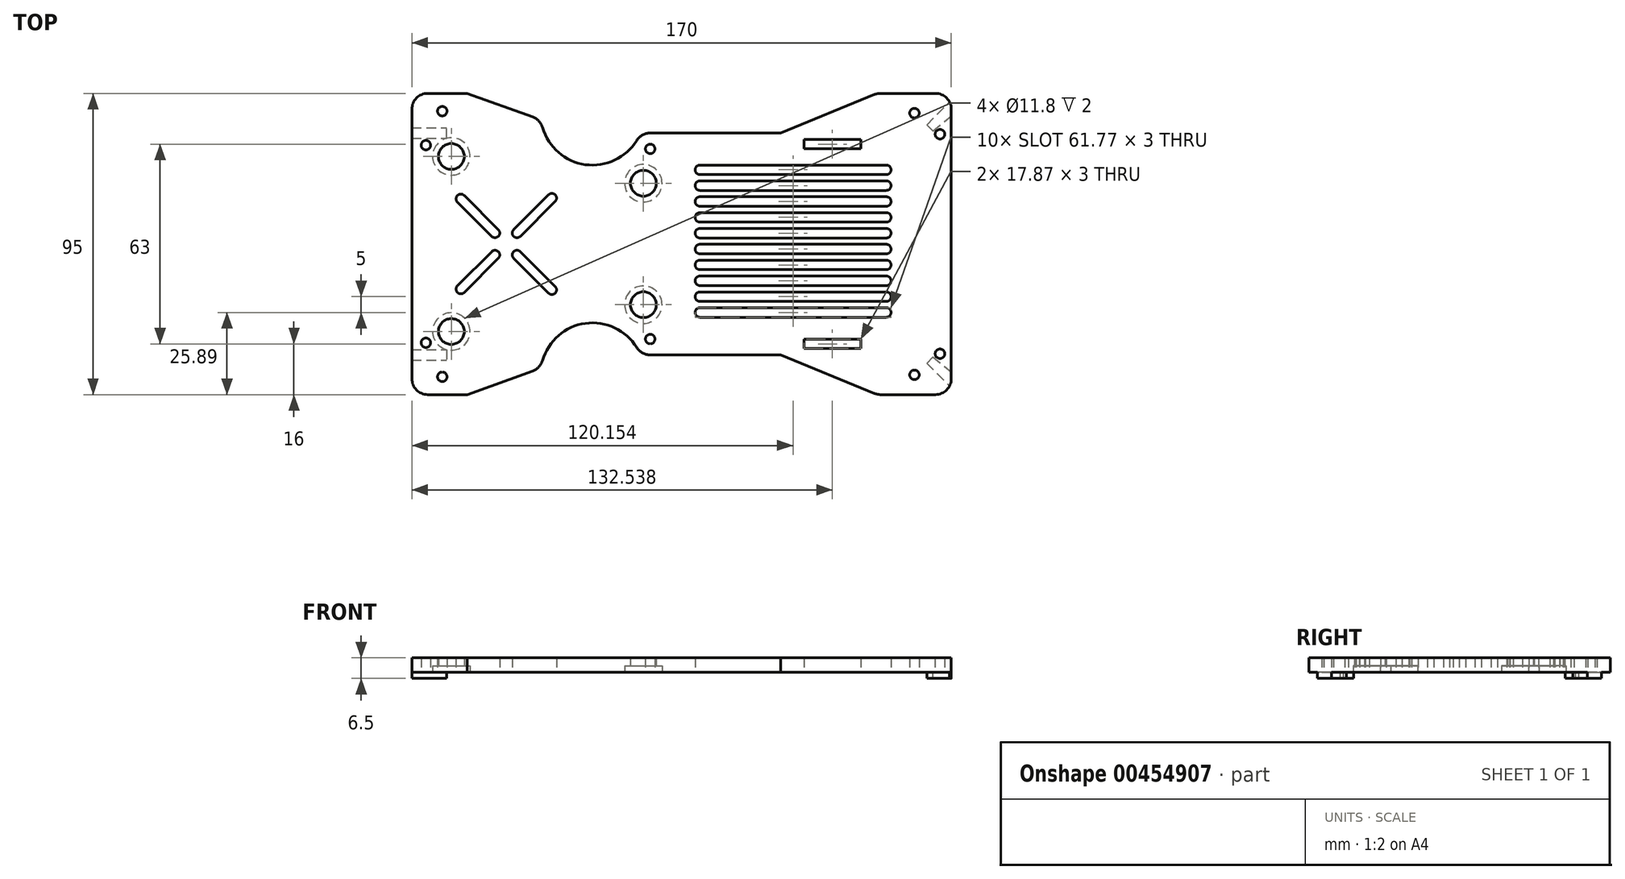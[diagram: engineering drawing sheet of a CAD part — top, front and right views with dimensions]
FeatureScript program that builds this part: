
annotation { "Feature Type Name" : "Feature", "Feature Type Description" : "" }
export const myFeature = defineFeature(function(context is Context, id is Id, definition is map)
    precondition{}
    {
        {
            var Q0;
            Q0=qCreatedBy(makeId("Top.planeOp"),FACE);
            var sketch = newSketch(context, id + "F0", { "sketchPlane" : qUnion([Q0])});
            skLineSegment(sketch, "E0.top", {"start": v(-158.33, 18) * mm, "end": v(-122.33, 18) * mm, "construction": true});
            skLineSegment(sketch, "E1.top", {"start": v(-2.46, 31.5) * mm, "end": v(-72.46, 31.5) * mm, "construction": true});
            skLineSegment(sketch, "E1.left", {"start": v(-2.46, 0) * mm, "end": v(-2.46, 31.5) * mm, "construction": true});
            skLineSegment(sketch, "E1.right", {"start": v(-72.46, 0) * mm, "end": v(-72.46, 31.5) * mm, "construction": true});
            skLineSegment(sketch, "E2.top", {"start": v(-5, 47.5) * mm, "end": v(-22.22, 47.5) * mm});
            skLineSegment(sketch, "E2.left", {"start": v(0, 35) * mm, "end": v(0, 42.5) * mm});
            skPoint(sketch, "E3.startSnap0", {"position": v(-23.2, 41.25) * mm});
            skPoint(sketch, "E3.startSnap1", {"position": v(-11.6, 47.5) * mm});
            skArc(sketch, "E4", {"start": v(-128.81, 36.72) * mm, "mid": v(-115.3, 25.02) * mm, "end": v(-99.14, 32.63) * mm});
            skLineSegment(sketch, "E5.trimOffspring", {"start": v(-94.88, 35) * mm, "end": v(-53.78, 35) * mm});
            skPoint(sketch, "E3.start.orphan", {"position": v(-11.6, 41.25) * mm});
            skCircle(sketch, "E6", {"center": v(-113.07, 41.25) * mm, "radius": 12.55 * mm, "construction": true});
            skLineSegment(sketch, "E7.top", {"start": v(-165, 47.5) * mm, "end": v(-149.65, 47.5) * mm});
            skLineSegment(sketch, "E7.left", {"start": v(-170, 35) * mm, "end": v(-170, 42.5) * mm});
            skLineSegment(sketch, "E8", {"start": v(-160.43, 41.87) * mm, "end": v(-136.46, 59) * mm, "construction": true});
            skPoint(sketch, "E8.startSnap0", {"position": v(-149.65, 47.5) * mm});
            skPoint(sketch, "E8.startSnap1", {"position": v(-170, 41.25) * mm});
            skLineSegment(sketch, "E9", {"start": v(-136.46, 59) * mm, "end": v(-62.44, 61.85) * mm, "construction": true});
            skLineSegment(sketch, "E10", {"start": v(-160.43, 41.87) * mm, "end": v(-62.44, 61.85) * mm, "construction": true});
            skCircle(sketch, "E11", {"center": v(-62.44, 61.85) * mm, "radius": 12.62 * mm, "construction": true});
            skLineSegment(sketch, "E12", {"start": v(-140.33, 0) * mm, "end": v(-158.33, 18) * mm, "construction": true});
            skLineSegment(sketch, "E13", {"start": v(-140.33, 0) * mm, "end": v(-122.33, 18) * mm, "construction": true});
            skArc(sketch, "E14", {"start": v(-153.5, 15.3) * mm, "mid": v(-155.63, 15.3) * mm, "end": v(-155.63, 13.18) * mm});
            skArc(sketch, "E15", {"start": v(-144.87, 2.42) * mm, "mid": v(-142.75, 2.42) * mm, "end": v(-142.75, 4.54) * mm});
            skArc(sketch, "E16", {"start": v(-137.91, 4.54) * mm, "mid": v(-137.91, 2.42) * mm, "end": v(-135.8, 2.42) * mm});
            skArc(sketch, "E17", {"start": v(-124.83, 13.38) * mm, "mid": v(-124.83, 15.5) * mm, "end": v(-126.95, 15.5) * mm});
            skLineSegment(sketch, "E18", {"start": v(-142.75, 4.54) * mm, "end": v(-153.5, 15.3) * mm});
            skLineSegment(sketch, "E19", {"start": v(-144.87, 2.42) * mm, "end": v(-155.63, 13.18) * mm});
            skLineSegment(sketch, "E20", {"start": v(-137.91, 4.54) * mm, "end": v(-126.95, 15.5) * mm});
            skLineSegment(sketch, "E21", {"start": v(-135.8, 2.42) * mm, "end": v(-124.83, 13.38) * mm});
            skLineSegment(sketch, "E22", {"start": v(-24.11, 47.13) * mm, "end": v(-53.78, 35) * mm});
            skCircle(sketch, "E23", {"center": v(-157.56, 27.6) * mm, "radius": 4.06 * mm});
            skCircle(sketch, "E24", {"center": v(-97.04, 19.15) * mm, "radius": 4.06 * mm});
            skPoint(sketch, "E2.bottom.end.orphan", {"position": v(-23.2, 35) * mm});
            skLineSegment(sketch, "E25.bottom", {"start": v(-28.53, 30) * mm, "end": v(-46.4, 30) * mm});
            skLineSegment(sketch, "E25.top", {"start": v(-28.53, 33) * mm, "end": v(-46.4, 33) * mm});
            skLineSegment(sketch, "E25.left", {"start": v(-28.53, 30) * mm, "end": v(-28.53, 33) * mm});
            skLineSegment(sketch, "E25.right", {"start": v(-46.4, 30) * mm, "end": v(-46.4, 33) * mm});
            skPoint(sketch, "E25.middle", {"position": v(-37.46, 31.5) * mm});
            skLineSegment(sketch, "E26", {"start": v(-131.92, 40.04) * mm, "end": v(-152.56, 47.5) * mm});
            skPoint(sketch, "E7.right.end.orphan", {"position": v(-129.3, 47.5) * mm});
            skPoint(sketch, "E27.visualSharp", {"position": v(-170, 47.5) * mm});
            skArc(sketch, "E27.filletArc", {"start": v(-165, 47.5) * mm, "mid": v(-168.54, 46.04) * mm, "end": v(-170, 42.5) * mm});
            skLineSegment(sketch, "E28", {"start": v(-2.46, 0) * mm, "end": v(-170, 0) * mm, "construction": true});
            skLineSegment(sketch, "E29", {"start": v(0, 35) * mm, "end": v(0, 0) * mm});
            skLineSegment(sketch, "E30", {"start": v(-170, 35) * mm, "end": v(-170, 0) * mm});
            skPoint(sketch, "E31.visualSharp", {"position": v(-129.3, 39.1) * mm});
            skArc(sketch, "E31.filletArc", {"start": v(-128.81, 36.72) * mm, "mid": v(-129.96, 38.75) * mm, "end": v(-131.92, 40.04) * mm});
            skPoint(sketch, "E32.visualSharp", {"position": v(-23.2, 47.5) * mm});
            skArc(sketch, "E32.filletArc", {"start": v(-22.22, 47.5) * mm, "mid": v(-23.19, 47.4) * mm, "end": v(-24.11, 47.13) * mm});
            skPoint(sketch, "E33.visualSharp", {"position": v(0, 47.5) * mm});
            skArc(sketch, "E33.filletArc", {"start": v(0, 42.5) * mm, "mid": v(-1.46, 46.04) * mm, "end": v(-5, 47.5) * mm});
            skPoint(sketch, "E34.visualSharp", {"position": v(-97.92, 35) * mm});
            skArc(sketch, "E34.filletArc", {"start": v(-94.88, 35) * mm, "mid": v(-97.32, 34.37) * mm, "end": v(-99.14, 32.63) * mm});
            skCircle(sketch, "E35", {"center": v(-94.88, 30) * mm, "radius": 1.5 * mm});
            skCircle(sketch, "E36", {"center": v(-165.6, 31.16) * mm, "radius": 1.5 * mm});
            skCircle(sketch, "E37", {"center": v(-3.57, 34.62) * mm, "radius": 1.5 * mm});
            skArc(sketch, "E38.MirrorCS", {"start": v(-22.22, -47.5) * mm, "mid": v(-23.19, -47.4) * mm, "end": v(-24.11, -47.13) * mm});
            skCircle(sketch, "E39.MirrorC", {"center": v(-94.88, -30) * mm, "radius": 1.5 * mm});
            skArc(sketch, "E40.MirrorCS", {"start": v(-137.91, -4.54) * mm, "mid": v(-137.91, -2.42) * mm, "end": v(-135.8, -2.42) * mm});
            skArc(sketch, "E41.MirrorCS", {"start": v(-144.87, -2.42) * mm, "mid": v(-142.75, -2.42) * mm, "end": v(-142.75, -4.54) * mm});
            skLineSegment(sketch, "E42.MirrorCS", {"start": v(-28.53, -30) * mm, "end": v(-28.53, -33) * mm});
            skArc(sketch, "E43.MirrorCS", {"start": v(-153.5, -15.3) * mm, "mid": v(-155.63, -15.3) * mm, "end": v(-155.63, -13.18) * mm});
            skArc(sketch, "E44.MirrorCS", {"start": v(-94.88, -35) * mm, "mid": v(-97.32, -34.37) * mm, "end": v(-99.14, -32.63) * mm});
            skLineSegment(sketch, "E45.MirrorCS", {"start": v(-46.4, -30) * mm, "end": v(-46.4, -33) * mm});
            skArc(sketch, "E46.MirrorCS", {"start": v(-124.83, -13.38) * mm, "mid": v(-124.83, -15.5) * mm, "end": v(-126.95, -15.5) * mm});
            skArc(sketch, "E47.MirrorCS", {"start": v(-128.81, -36.72) * mm, "mid": v(-129.96, -38.75) * mm, "end": v(-131.92, -40.04) * mm});
            skArc(sketch, "E48.MirrorCS", {"start": v(-165, -47.5) * mm, "mid": v(-168.54, -46.04) * mm, "end": v(-170, -42.5) * mm});
            skCircle(sketch, "E49.MirrorC", {"center": v(-3.57, -34.62) * mm, "radius": 1.5 * mm});
            skArc(sketch, "E50.MirrorCS", {"start": v(0, -42.5) * mm, "mid": v(-1.46, -46.04) * mm, "end": v(-5, -47.5) * mm});
            skCircle(sketch, "E51.MirrorC", {"center": v(-165.6, -31.16) * mm, "radius": 1.5 * mm});
            skLineSegment(sketch, "E52.MirrorCS", {"start": v(-170, -35) * mm, "end": v(-170, -42.5) * mm});
            skLineSegment(sketch, "E53.MirrorCS", {"start": v(-2.46, -31.5) * mm, "end": v(-72.46, -31.5) * mm, "construction": true});
            skLineSegment(sketch, "E54.MirrorCS", {"start": v(-24.11, -47.13) * mm, "end": v(-53.78, -35) * mm});
            skLineSegment(sketch, "E55.MirrorCS", {"start": v(-165, -47.5) * mm, "end": v(-149.65, -47.5) * mm});
            skCircle(sketch, "E56.MirrorC", {"center": v(-157.56, -27.6) * mm, "radius": 4.06 * mm});
            skLineSegment(sketch, "E57.MirrorCS", {"start": v(-135.8, -2.42) * mm, "end": v(-124.83, -13.38) * mm});
            skPoint(sketch, "E58.MirrorP", {"position": v(-37.46, -31.5) * mm});
            skPoint(sketch, "E59.MirrorP", {"position": v(-23.2, -35) * mm});
            skPoint(sketch, "E60.MirrorP", {"position": v(-129.3, -39.1) * mm});
            skPoint(sketch, "E61.MirrorP", {"position": v(-11.6, -41.25) * mm});
            skLineSegment(sketch, "E62.MirrorCS", {"start": v(-72.46, 0) * mm, "end": v(-72.46, -31.5) * mm, "construction": true});
            skLineSegment(sketch, "E63.MirrorCS", {"start": v(-5, -47.5) * mm, "end": v(-22.22, -47.5) * mm});
            skLineSegment(sketch, "E64.MirrorCS", {"start": v(-94.88, -35) * mm, "end": v(-53.78, -35) * mm});
            skArc(sketch, "E65.MirrorCS", {"start": v(-128.81, -36.72) * mm, "mid": v(-115.3, -25.02) * mm, "end": v(-99.14, -32.63) * mm});
            skPoint(sketch, "E66.MirrorP", {"position": v(-149.65, -47.5) * mm});
            skPoint(sketch, "E67.MirrorP", {"position": v(-23.2, -47.5) * mm});
            skLineSegment(sketch, "E68.MirrorCS", {"start": v(-170, -35) * mm, "end": v(-170, 0) * mm});
            skLineSegment(sketch, "E69.MirrorCS", {"start": v(0, -35) * mm, "end": v(0, -42.5) * mm});
            skPoint(sketch, "E70.MirrorP", {"position": v(-129.3, -47.5) * mm});
            skCircle(sketch, "E71.MirrorC", {"center": v(-113.07, -41.25) * mm, "radius": 12.55 * mm, "construction": true});
            skLineSegment(sketch, "E72.MirrorCS", {"start": v(-160.43, -41.87) * mm, "end": v(-136.46, -59) * mm, "construction": true});
            skLineSegment(sketch, "E73.MirrorCS", {"start": v(-158.33, -18) * mm, "end": v(-122.33, -18) * mm, "construction": true});
            skPoint(sketch, "E74.MirrorP", {"position": v(0, -47.5) * mm});
            skLineSegment(sketch, "E75.MirrorCS", {"start": v(-131.92, -40.04) * mm, "end": v(-152.56, -47.5) * mm});
            skPoint(sketch, "E76.MirrorP", {"position": v(-11.6, -47.5) * mm});
            skLineSegment(sketch, "E77.MirrorCS", {"start": v(-140.33, 0) * mm, "end": v(-122.33, -18) * mm, "construction": true});
            skLineSegment(sketch, "E78.MirrorCS", {"start": v(-2.46, 0) * mm, "end": v(-2.46, -31.5) * mm, "construction": true});
            skLineSegment(sketch, "E79.MirrorCS", {"start": v(-28.53, -30) * mm, "end": v(-46.4, -30) * mm});
            skPoint(sketch, "E80.MirrorP", {"position": v(-170, -41.25) * mm});
            skLineSegment(sketch, "E81.MirrorCS", {"start": v(-140.33, 0) * mm, "end": v(-158.33, -18) * mm, "construction": true});
            skLineSegment(sketch, "E82.MirrorCS", {"start": v(-28.53, -33) * mm, "end": v(-46.4, -33) * mm});
            skPoint(sketch, "E83.MirrorP", {"position": v(-97.92, -35) * mm});
            skLineSegment(sketch, "E84.MirrorCS", {"start": v(-160.43, -41.87) * mm, "end": v(-62.44, -61.85) * mm, "construction": true});
            skLineSegment(sketch, "E85.MirrorCS", {"start": v(0, -35) * mm, "end": v(0, 0) * mm});
            skLineSegment(sketch, "E86.MirrorCS", {"start": v(-136.46, -59) * mm, "end": v(-62.44, -61.85) * mm, "construction": true});
            skPoint(sketch, "E87.MirrorP", {"position": v(-170, -47.5) * mm});
            skCircle(sketch, "E88.MirrorC", {"center": v(-97.04, -19.15) * mm, "radius": 4.06 * mm});
            skLineSegment(sketch, "E89.MirrorCS", {"start": v(-142.75, -4.54) * mm, "end": v(-153.5, -15.3) * mm});
            skLineSegment(sketch, "E90.MirrorCS", {"start": v(-137.91, -4.54) * mm, "end": v(-126.95, -15.5) * mm});
            skLineSegment(sketch, "E91.MirrorCS", {"start": v(-144.87, -2.42) * mm, "end": v(-155.63, -13.18) * mm});
            skCircle(sketch, "E92.MirrorC", {"center": v(-62.44, -61.85) * mm, "radius": 12.62 * mm, "construction": true});
            skCircle(sketch, "E93", {"center": v(-11.6, 41.25) * mm, "radius": 1.5 * mm});
            skCircle(sketch, "E94", {"center": v(-160.43, 41.87) * mm, "radius": 1.5 * mm});
            skCircle(sketch, "E95.MirrorC", {"center": v(-11.6, -41.25) * mm, "radius": 1.5 * mm});
            skCircle(sketch, "E96.MirrorC", {"center": v(-160.43, -41.87) * mm, "radius": 1.5 * mm});
            skSolve(sketch);
        }
        {
            var Q0;
            Q0 = qSketchRegion(id + "F0", true);
            extrude(context, id + "F1", {"entities" : qUnion([Q0]), "depth" : 4.5 * mm});
        }
        {
            var Q0;
            Q0=makeQuery(id+"F1.opExtrude","CAP_FACE",FACE,{"disambiguationData":[OSD([sQuery(id+"F0.wireOp",EDGE,"E2.top"),sQuery(id+"F0.wireOp",EDGE,"E2.left"),sQuery(id+"F0.wireOp",EDGE,"E4"),sQuery(id+"F0.wireOp",EDGE,"E5.trimOffspring"),sQuery(id+"F0.wireOp",EDGE,"E7.top"),sQuery(id+"F0.wireOp",EDGE,"E7.left"),sQuery(id+"F0.wireOp",EDGE,"E14"),sQuery(id+"F0.wireOp",EDGE,"E15"),sQuery(id+"F0.wireOp",EDGE,"E16"),sQuery(id+"F0.wireOp",EDGE,"E17"),sQuery(id+"F0.wireOp",EDGE,"E18"),sQuery(id+"F0.wireOp",EDGE,"E19"),sQuery(id+"F0.wireOp",EDGE,"E20"),sQuery(id+"F0.wireOp",EDGE,"E21"),sQuery(id+"F0.wireOp",EDGE,"E22"),sQuery(id+"F0.wireOp",EDGE,"E23"),sQuery(id+"F0.wireOp",EDGE,"E24"),sQuery(id+"F0.wireOp",EDGE,"E25.bottom"),sQuery(id+"F0.wireOp",EDGE,"E25.top"),sQuery(id+"F0.wireOp",EDGE,"E25.left"),sQuery(id+"F0.wireOp",EDGE,"E25.right"),sQuery(id+"F0.wireOp",EDGE,"E26"),sQuery(id+"F0.wireOp",EDGE,"E27.filletArc"),sQuery(id+"F0.wireOp",EDGE,"E29"),sQuery(id+"F0.wireOp",EDGE,"E30"),sQuery(id+"F0.wireOp",EDGE,"E31.filletArc"),sQuery(id+"F0.wireOp",EDGE,"E32.filletArc"),sQuery(id+"F0.wireOp",EDGE,"E33.filletArc"),sQuery(id+"F0.wireOp",EDGE,"E34.filletArc"),sQuery(id+"F0.wireOp",EDGE,"E35"),sQuery(id+"F0.wireOp",EDGE,"E36"),sQuery(id+"F0.wireOp",EDGE,"E37"),sQuery(id+"F0.wireOp",EDGE,"dc92d004-a6ad-41b4-b321-0510745f16cf0.MirrorC"),sQuery(id+"F0.wireOp",EDGE,"E38.MirrorCS"),sQuery(id+"F0.wireOp",EDGE,"E39.MirrorC"),sQuery(id+"F0.wireOp",EDGE,"E40.MirrorCS"),sQuery(id+"F0.wireOp",EDGE,"E41.MirrorCS"),sQuery(id+"F0.wireOp",EDGE,"E42.MirrorCS"),sQuery(id+"F0.wireOp",EDGE,"E43.MirrorCS"),sQuery(id+"F0.wireOp",EDGE,"E44.MirrorCS"),sQuery(id+"F0.wireOp",EDGE,"E45.MirrorCS"),sQuery(id+"F0.wireOp",EDGE,"E46.MirrorCS"),sQuery(id+"F0.wireOp",EDGE,"E47.MirrorCS"),sQuery(id+"F0.wireOp",EDGE,"E48.MirrorCS"),sQuery(id+"F0.wireOp",EDGE,"E49.MirrorC"),sQuery(id+"F0.wireOp",EDGE,"E50.MirrorCS"),sQuery(id+"F0.wireOp",EDGE,"E51.MirrorC"),sQuery(id+"F0.wireOp",EDGE,"E52.MirrorCS"),sQuery(id+"F0.wireOp",EDGE,"E54.MirrorCS"),sQuery(id+"F0.wireOp",EDGE,"E55.MirrorCS"),sQuery(id+"F0.wireOp",EDGE,"E56.MirrorC"),sQuery(id+"F0.wireOp",EDGE,"E57.MirrorCS"),sQuery(id+"F0.wireOp",EDGE,"E63.MirrorCS"),sQuery(id+"F0.wireOp",EDGE,"E64.MirrorCS"),sQuery(id+"F0.wireOp",EDGE,"E65.MirrorCS"),sQuery(id+"F0.wireOp",EDGE,"E68.MirrorCS"),sQuery(id+"F0.wireOp",EDGE,"E69.MirrorCS"),sQuery(id+"F0.wireOp",EDGE,"E75.MirrorCS"),sQuery(id+"F0.wireOp",EDGE,"E79.MirrorCS"),sQuery(id+"F0.wireOp",EDGE,"E82.MirrorCS"),sQuery(id+"F0.wireOp",EDGE,"E85.MirrorCS"),sQuery(id+"F0.wireOp",EDGE,"E88.MirrorC"),sQuery(id+"F0.wireOp",EDGE,"E89.MirrorCS"),sQuery(id+"F0.wireOp",EDGE,"E90.MirrorCS"),sQuery(id+"F0.wireOp",EDGE,"E91.MirrorCS"),sQuery(id+"F0.wireOp",EDGE,"E93"),sQuery(id+"F0.wireOp",EDGE,"E94"),sQuery(id+"F0.wireOp",EDGE,"E95.MirrorC"),sQuery(id+"F0.wireOp",EDGE,"E96.MirrorC")])],"isStart":true});
            var sketch = newSketch(context, id + "F2", { "sketchPlane" : qUnion([Q0])});
            skLineSegment(sketch, "E97.bottom", {"start": v(-170, 33.34) * mm, "end": v(-159, 33.34) * mm});
            skLineSegment(sketch, "E97.top", {"start": v(-170, 36.59) * mm, "end": v(-159, 36.59) * mm});
            skLineSegment(sketch, "E97.left", {"start": v(-170, 33.34) * mm, "end": v(-170, 36.59) * mm});
            skLineSegment(sketch, "E97.right", {"start": v(-159, 33.34) * mm, "end": v(-159, 36.59) * mm});
            skLineSegment(sketch, "E98", {"start": v(-160.43, 41.87) * mm, "end": v(-160.43, 36.87) * mm, "construction": true});
            skLineSegment(sketch, "E99", {"start": v(-11.6, 41.25) * mm, "end": v(-8.07, 37.71) * mm, "construction": true});
            skLineSegment(sketch, "E100", {"start": v(-11.6, 41.25) * mm, "end": v(0, 41.25) * mm, "construction": true});
            skLineSegment(sketch, "E101", {"start": v(-7.7, 37.6) * mm, "end": v(-0.54, 44.75) * mm});
            skLineSegment(sketch, "E102", {"start": v(-7.7, 37.6) * mm, "end": v(-5.77, 35.67) * mm});
            skLineSegment(sketch, "E103", {"start": v(-5.77, 35.67) * mm, "end": v(0, 40.31) * mm});
            skArc(sketch, "E104.0", {"start": v(0, 42.5) * mm, "mid": v(-0.14, 43.66) * mm, "end": v(-0.54, 44.75) * mm});
            skLineSegment(sketch, "E105.0", {"start": v(0, 40.31) * mm, "end": v(0, 42.5) * mm});
            skPoint(sketch, "E106.orphan", {"position": v(-5, 47.5) * mm});
            skPoint(sketch, "E107.orphan", {"position": v(0, -42.5) * mm});
            skLineSegment(sketch, "E108", {"start": v(-170, 0) * mm, "end": v(0, 0) * mm, "construction": true});
            skLineSegment(sketch, "E109.MirrorCS", {"start": v(0, -40.31) * mm, "end": v(0, -42.5) * mm});
            skArc(sketch, "E110.MirrorCS", {"start": v(0, -42.5) * mm, "mid": v(-0.14, -43.66) * mm, "end": v(-0.54, -44.75) * mm});
            skLineSegment(sketch, "E111.MirrorCS", {"start": v(-7.7, -37.6) * mm, "end": v(-5.77, -35.67) * mm});
            skLineSegment(sketch, "E112.MirrorCS", {"start": v(-170, -33.34) * mm, "end": v(-170, -36.59) * mm});
            skLineSegment(sketch, "E113.MirrorCS", {"start": v(-159, -33.34) * mm, "end": v(-159, -36.59) * mm});
            skLineSegment(sketch, "E114.MirrorCS", {"start": v(-11.6, -41.25) * mm, "end": v(-8.07, -37.71) * mm, "construction": true});
            skLineSegment(sketch, "E115.MirrorCS", {"start": v(-5.77, -35.67) * mm, "end": v(0, -40.31) * mm});
            skLineSegment(sketch, "E116.MirrorCS", {"start": v(-11.6, -41.25) * mm, "end": v(0, -41.25) * mm, "construction": true});
            skLineSegment(sketch, "E117.MirrorCS", {"start": v(-160.43, -41.87) * mm, "end": v(-160.43, -36.87) * mm, "construction": true});
            skLineSegment(sketch, "E118.MirrorCS", {"start": v(-7.7, -37.6) * mm, "end": v(-0.54, -44.75) * mm});
            skPoint(sketch, "E119.MirrorP", {"position": v(-5, -47.5) * mm});
            skLineSegment(sketch, "E120.MirrorCS", {"start": v(-170, -33.34) * mm, "end": v(-159, -33.34) * mm});
            skLineSegment(sketch, "E121.MirrorCS", {"start": v(-170, -36.59) * mm, "end": v(-159, -36.59) * mm});
            skSolve(sketch);
        }
        {
            var Q0;
            Q0 = qSketchRegion(id + "F2", true);
            extrude(context, id + "F3", {"entities" : qUnion([Q0]), "operationType" : NewBodyOperationType.ADD, "depth" : 2 * mm});
        }
        {
            var Q0;
            Q0=makeQuery(id+"F1.opExtrude","CAP_FACE",FACE,{"disambiguationData":[OSD([sQuery(id+"F0.wireOp",EDGE,"E2.top"),sQuery(id+"F0.wireOp",EDGE,"E2.left"),sQuery(id+"F0.wireOp",EDGE,"E4"),sQuery(id+"F0.wireOp",EDGE,"E5.trimOffspring"),sQuery(id+"F0.wireOp",EDGE,"E7.top"),sQuery(id+"F0.wireOp",EDGE,"E7.left"),sQuery(id+"F0.wireOp",EDGE,"E14"),sQuery(id+"F0.wireOp",EDGE,"E15"),sQuery(id+"F0.wireOp",EDGE,"E16"),sQuery(id+"F0.wireOp",EDGE,"E17"),sQuery(id+"F0.wireOp",EDGE,"E18"),sQuery(id+"F0.wireOp",EDGE,"E19"),sQuery(id+"F0.wireOp",EDGE,"E20"),sQuery(id+"F0.wireOp",EDGE,"E21"),sQuery(id+"F0.wireOp",EDGE,"E22"),sQuery(id+"F0.wireOp",EDGE,"E23"),sQuery(id+"F0.wireOp",EDGE,"E24"),sQuery(id+"F0.wireOp",EDGE,"E25.bottom"),sQuery(id+"F0.wireOp",EDGE,"E25.top"),sQuery(id+"F0.wireOp",EDGE,"E25.left"),sQuery(id+"F0.wireOp",EDGE,"E25.right"),sQuery(id+"F0.wireOp",EDGE,"E26"),sQuery(id+"F0.wireOp",EDGE,"E27.filletArc"),sQuery(id+"F0.wireOp",EDGE,"E29"),sQuery(id+"F0.wireOp",EDGE,"E30"),sQuery(id+"F0.wireOp",EDGE,"E31.filletArc"),sQuery(id+"F0.wireOp",EDGE,"E32.filletArc"),sQuery(id+"F0.wireOp",EDGE,"E33.filletArc"),sQuery(id+"F0.wireOp",EDGE,"E34.filletArc"),sQuery(id+"F0.wireOp",EDGE,"E35"),sQuery(id+"F0.wireOp",EDGE,"E36"),sQuery(id+"F0.wireOp",EDGE,"E37"),sQuery(id+"F0.wireOp",EDGE,"dc92d004-a6ad-41b4-b321-0510745f16cf0.MirrorC"),sQuery(id+"F0.wireOp",EDGE,"E38.MirrorCS"),sQuery(id+"F0.wireOp",EDGE,"E39.MirrorC"),sQuery(id+"F0.wireOp",EDGE,"E40.MirrorCS"),sQuery(id+"F0.wireOp",EDGE,"E41.MirrorCS"),sQuery(id+"F0.wireOp",EDGE,"E42.MirrorCS"),sQuery(id+"F0.wireOp",EDGE,"E43.MirrorCS"),sQuery(id+"F0.wireOp",EDGE,"E44.MirrorCS"),sQuery(id+"F0.wireOp",EDGE,"E45.MirrorCS"),sQuery(id+"F0.wireOp",EDGE,"E46.MirrorCS"),sQuery(id+"F0.wireOp",EDGE,"E47.MirrorCS"),sQuery(id+"F0.wireOp",EDGE,"E48.MirrorCS"),sQuery(id+"F0.wireOp",EDGE,"E49.MirrorC"),sQuery(id+"F0.wireOp",EDGE,"E50.MirrorCS"),sQuery(id+"F0.wireOp",EDGE,"E51.MirrorC"),sQuery(id+"F0.wireOp",EDGE,"E52.MirrorCS"),sQuery(id+"F0.wireOp",EDGE,"E54.MirrorCS"),sQuery(id+"F0.wireOp",EDGE,"E55.MirrorCS"),sQuery(id+"F0.wireOp",EDGE,"E56.MirrorC"),sQuery(id+"F0.wireOp",EDGE,"E57.MirrorCS"),sQuery(id+"F0.wireOp",EDGE,"E63.MirrorCS"),sQuery(id+"F0.wireOp",EDGE,"E64.MirrorCS"),sQuery(id+"F0.wireOp",EDGE,"E65.MirrorCS"),sQuery(id+"F0.wireOp",EDGE,"E68.MirrorCS"),sQuery(id+"F0.wireOp",EDGE,"E69.MirrorCS"),sQuery(id+"F0.wireOp",EDGE,"E75.MirrorCS"),sQuery(id+"F0.wireOp",EDGE,"E79.MirrorCS"),sQuery(id+"F0.wireOp",EDGE,"E82.MirrorCS"),sQuery(id+"F0.wireOp",EDGE,"E85.MirrorCS"),sQuery(id+"F0.wireOp",EDGE,"E88.MirrorC"),sQuery(id+"F0.wireOp",EDGE,"E89.MirrorCS"),sQuery(id+"F0.wireOp",EDGE,"E90.MirrorCS"),sQuery(id+"F0.wireOp",EDGE,"E91.MirrorCS"),sQuery(id+"F0.wireOp",EDGE,"E93"),sQuery(id+"F0.wireOp",EDGE,"E94"),sQuery(id+"F0.wireOp",EDGE,"E95.MirrorC"),sQuery(id+"F0.wireOp",EDGE,"E96.MirrorC")])],"isStart":true});
            var sketch = newSketch(context, id + "F4", { "sketchPlane" : qUnion([Q0])});
            skCircle(sketch, "E122", {"center": v(-97.04, 19.15) * mm, "radius": 5.9 * mm});
            skCircle(sketch, "E123", {"center": v(-157.56, 27.6) * mm, "radius": 5.9 * mm});
            skCircle(sketch, "E124", {"center": v(-97.04, -19.15) * mm, "radius": 5.9 * mm});
            skCircle(sketch, "E125", {"center": v(-157.56, -27.6) * mm, "radius": 5.9 * mm});
            skSolve(sketch);
        }
        {
            var Q0;
            Q0 = qSketchRegion(id + "F4", true);
            extrude(context, id + "F5", {"entities" : qUnion([Q0]), "operationType" : NewBodyOperationType.REMOVE, "oppositeDirection" : true, "depth" : 2 * mm});
        }
        {
            var Q0;
            Q0=makeQuery(id+"F1.opExtrude","CAP_FACE",FACE,{"disambiguationData":[OSD([sQuery(id+"F0.wireOp",EDGE,"E2.top"),sQuery(id+"F0.wireOp",EDGE,"E2.left"),sQuery(id+"F0.wireOp",EDGE,"E4"),sQuery(id+"F0.wireOp",EDGE,"E5.trimOffspring"),sQuery(id+"F0.wireOp",EDGE,"E7.top"),sQuery(id+"F0.wireOp",EDGE,"E7.left"),sQuery(id+"F0.wireOp",EDGE,"E14"),sQuery(id+"F0.wireOp",EDGE,"E15"),sQuery(id+"F0.wireOp",EDGE,"E16"),sQuery(id+"F0.wireOp",EDGE,"E17"),sQuery(id+"F0.wireOp",EDGE,"E18"),sQuery(id+"F0.wireOp",EDGE,"E19"),sQuery(id+"F0.wireOp",EDGE,"E20"),sQuery(id+"F0.wireOp",EDGE,"E21"),sQuery(id+"F0.wireOp",EDGE,"E22"),sQuery(id+"F0.wireOp",EDGE,"E23"),sQuery(id+"F0.wireOp",EDGE,"E24"),sQuery(id+"F0.wireOp",EDGE,"E25.bottom"),sQuery(id+"F0.wireOp",EDGE,"E25.top"),sQuery(id+"F0.wireOp",EDGE,"E25.left"),sQuery(id+"F0.wireOp",EDGE,"E25.right"),sQuery(id+"F0.wireOp",EDGE,"E26"),sQuery(id+"F0.wireOp",EDGE,"E27.filletArc"),sQuery(id+"F0.wireOp",EDGE,"E29"),sQuery(id+"F0.wireOp",EDGE,"E30"),sQuery(id+"F0.wireOp",EDGE,"E31.filletArc"),sQuery(id+"F0.wireOp",EDGE,"E32.filletArc"),sQuery(id+"F0.wireOp",EDGE,"E33.filletArc"),sQuery(id+"F0.wireOp",EDGE,"E34.filletArc"),sQuery(id+"F0.wireOp",EDGE,"E35"),sQuery(id+"F0.wireOp",EDGE,"E36"),sQuery(id+"F0.wireOp",EDGE,"E37"),sQuery(id+"F0.wireOp",EDGE,"dc92d004-a6ad-41b4-b321-0510745f16cf0.MirrorC"),sQuery(id+"F0.wireOp",EDGE,"E38.MirrorCS"),sQuery(id+"F0.wireOp",EDGE,"E39.MirrorC"),sQuery(id+"F0.wireOp",EDGE,"E40.MirrorCS"),sQuery(id+"F0.wireOp",EDGE,"E41.MirrorCS"),sQuery(id+"F0.wireOp",EDGE,"E42.MirrorCS"),sQuery(id+"F0.wireOp",EDGE,"E43.MirrorCS"),sQuery(id+"F0.wireOp",EDGE,"E44.MirrorCS"),sQuery(id+"F0.wireOp",EDGE,"E45.MirrorCS"),sQuery(id+"F0.wireOp",EDGE,"E46.MirrorCS"),sQuery(id+"F0.wireOp",EDGE,"E47.MirrorCS"),sQuery(id+"F0.wireOp",EDGE,"E48.MirrorCS"),sQuery(id+"F0.wireOp",EDGE,"E49.MirrorC"),sQuery(id+"F0.wireOp",EDGE,"E50.MirrorCS"),sQuery(id+"F0.wireOp",EDGE,"E51.MirrorC"),sQuery(id+"F0.wireOp",EDGE,"E52.MirrorCS"),sQuery(id+"F0.wireOp",EDGE,"E54.MirrorCS"),sQuery(id+"F0.wireOp",EDGE,"E55.MirrorCS"),sQuery(id+"F0.wireOp",EDGE,"E56.MirrorC"),sQuery(id+"F0.wireOp",EDGE,"E57.MirrorCS"),sQuery(id+"F0.wireOp",EDGE,"E63.MirrorCS"),sQuery(id+"F0.wireOp",EDGE,"E64.MirrorCS"),sQuery(id+"F0.wireOp",EDGE,"E65.MirrorCS"),sQuery(id+"F0.wireOp",EDGE,"E68.MirrorCS"),sQuery(id+"F0.wireOp",EDGE,"E69.MirrorCS"),sQuery(id+"F0.wireOp",EDGE,"E75.MirrorCS"),sQuery(id+"F0.wireOp",EDGE,"E79.MirrorCS"),sQuery(id+"F0.wireOp",EDGE,"E82.MirrorCS"),sQuery(id+"F0.wireOp",EDGE,"E85.MirrorCS"),sQuery(id+"F0.wireOp",EDGE,"E88.MirrorC"),sQuery(id+"F0.wireOp",EDGE,"E89.MirrorCS"),sQuery(id+"F0.wireOp",EDGE,"E90.MirrorCS"),sQuery(id+"F0.wireOp",EDGE,"E91.MirrorCS"),sQuery(id+"F0.wireOp",EDGE,"E93"),sQuery(id+"F0.wireOp",EDGE,"E94"),sQuery(id+"F0.wireOp",EDGE,"E95.MirrorC"),sQuery(id+"F0.wireOp",EDGE,"E96.MirrorC")])],"isStart":true});
            var sketch = newSketch(context, id + "F6", { "sketchPlane" : qUnion([Q0])});
            skArc(sketch, "E126.0.startCap", {"start": v(-79.23, 20.11) * mm, "mid": v(-80.73, 21.61) * mm, "end": v(-79.23, 23.11) * mm});
            skArc(sketch, "E126.0.endCap", {"start": v(-20.46, 23.11) * mm, "mid": v(-18.96, 21.61) * mm, "end": v(-20.46, 20.11) * mm});
            skLineSegment(sketch, "E126.0.left", {"start": v(-79.23, 23.11) * mm, "end": v(-20.46, 23.11) * mm});
            skLineSegment(sketch, "E126.0.right", {"start": v(-79.23, 20.11) * mm, "end": v(-20.46, 20.11) * mm});
            skLineSegment(sketch, "E127.0.1.0", {"start": v(-79.23, 18.11) * mm, "end": v(-20.46, 18.11) * mm});
            skArc(sketch, "E127.0.1.1", {"start": v(-79.23, 15.11) * mm, "mid": v(-80.73, 16.61) * mm, "end": v(-79.23, 18.11) * mm});
            skLineSegment(sketch, "E127.0.1.2", {"start": v(-79.23, 15.11) * mm, "end": v(-20.46, 15.11) * mm});
            skArc(sketch, "E127.0.1.3", {"start": v(-20.46, 18.11) * mm, "mid": v(-18.96, 16.61) * mm, "end": v(-20.46, 15.11) * mm});
            skLineSegment(sketch, "E127.0.2.0", {"start": v(-79.23, 13.11) * mm, "end": v(-20.46, 13.11) * mm});
            skArc(sketch, "E127.0.2.1", {"start": v(-79.23, 10.11) * mm, "mid": v(-80.73, 11.61) * mm, "end": v(-79.23, 13.11) * mm});
            skLineSegment(sketch, "E127.0.2.2", {"start": v(-79.23, 10.11) * mm, "end": v(-20.46, 10.11) * mm});
            skArc(sketch, "E127.0.2.3", {"start": v(-20.46, 13.11) * mm, "mid": v(-18.96, 11.61) * mm, "end": v(-20.46, 10.11) * mm});
            skLineSegment(sketch, "E127.0.3.0", {"start": v(-79.23, 8.11) * mm, "end": v(-20.46, 8.11) * mm});
            skArc(sketch, "E127.0.3.1", {"start": v(-79.23, 5.11) * mm, "mid": v(-80.73, 6.61) * mm, "end": v(-79.23, 8.11) * mm});
            skLineSegment(sketch, "E127.0.3.2", {"start": v(-79.23, 5.11) * mm, "end": v(-20.46, 5.11) * mm});
            skArc(sketch, "E127.0.3.3", {"start": v(-20.46, 8.11) * mm, "mid": v(-18.96, 6.61) * mm, "end": v(-20.46, 5.11) * mm});
            skLineSegment(sketch, "E127.0.4.0", {"start": v(-79.23, 3.11) * mm, "end": v(-20.46, 3.11) * mm});
            skArc(sketch, "E127.0.4.1", {"start": v(-79.23, 0.11) * mm, "mid": v(-80.73, 1.61) * mm, "end": v(-79.23, 3.11) * mm});
            skLineSegment(sketch, "E127.0.4.2", {"start": v(-79.23, 0.11) * mm, "end": v(-20.46, 0.11) * mm});
            skArc(sketch, "E127.0.4.3", {"start": v(-20.46, 3.11) * mm, "mid": v(-18.96, 1.61) * mm, "end": v(-20.46, 0.11) * mm});
            skLineSegment(sketch, "E127.0.5.0", {"start": v(-79.23, -1.89) * mm, "end": v(-20.46, -1.89) * mm});
            skArc(sketch, "E127.0.5.1", {"start": v(-79.23, -4.89) * mm, "mid": v(-80.73, -3.39) * mm, "end": v(-79.23, -1.89) * mm});
            skLineSegment(sketch, "E127.0.5.2", {"start": v(-79.23, -4.89) * mm, "end": v(-20.46, -4.89) * mm});
            skArc(sketch, "E127.0.5.3", {"start": v(-20.46, -1.89) * mm, "mid": v(-18.96, -3.39) * mm, "end": v(-20.46, -4.89) * mm});
            skLineSegment(sketch, "E127.0.6.0", {"start": v(-79.23, -6.89) * mm, "end": v(-20.46, -6.89) * mm});
            skArc(sketch, "E127.0.6.1", {"start": v(-79.23, -9.89) * mm, "mid": v(-80.73, -8.39) * mm, "end": v(-79.23, -6.89) * mm});
            skLineSegment(sketch, "E127.0.6.2", {"start": v(-79.23, -9.89) * mm, "end": v(-20.46, -9.89) * mm});
            skArc(sketch, "E127.0.6.3", {"start": v(-20.46, -6.89) * mm, "mid": v(-18.96, -8.39) * mm, "end": v(-20.46, -9.89) * mm});
            skLineSegment(sketch, "E127.0.7.0", {"start": v(-79.23, -11.89) * mm, "end": v(-20.46, -11.89) * mm});
            skArc(sketch, "E127.0.7.1", {"start": v(-79.23, -14.89) * mm, "mid": v(-80.73, -13.39) * mm, "end": v(-79.23, -11.89) * mm});
            skLineSegment(sketch, "E127.0.7.2", {"start": v(-79.23, -14.89) * mm, "end": v(-20.46, -14.89) * mm});
            skArc(sketch, "E127.0.7.3", {"start": v(-20.46, -11.89) * mm, "mid": v(-18.96, -13.39) * mm, "end": v(-20.46, -14.89) * mm});
            skLineSegment(sketch, "E127.0.8.0", {"start": v(-79.23, -16.89) * mm, "end": v(-20.46, -16.89) * mm});
            skArc(sketch, "E127.0.8.1", {"start": v(-79.23, -19.89) * mm, "mid": v(-80.73, -18.39) * mm, "end": v(-79.23, -16.89) * mm});
            skLineSegment(sketch, "E127.0.8.2", {"start": v(-79.23, -19.89) * mm, "end": v(-20.46, -19.89) * mm});
            skArc(sketch, "E127.0.8.3", {"start": v(-20.46, -16.89) * mm, "mid": v(-18.96, -18.39) * mm, "end": v(-20.46, -19.89) * mm});
            skLineSegment(sketch, "E127.0.9.0", {"start": v(-79.23, -21.89) * mm, "end": v(-20.46, -21.89) * mm});
            skArc(sketch, "E127.0.9.1", {"start": v(-79.23, -24.89) * mm, "mid": v(-80.73, -23.39) * mm, "end": v(-79.23, -21.89) * mm});
            skLineSegment(sketch, "E127.0.9.2", {"start": v(-79.23, -24.89) * mm, "end": v(-20.46, -24.89) * mm});
            skArc(sketch, "E127.0.9.3", {"start": v(-20.46, -21.89) * mm, "mid": v(-18.96, -23.39) * mm, "end": v(-20.46, -24.89) * mm});
            skLineSegment(sketch, "E127.direction1", {"start": v(-79.23, 23.11) * mm, "end": v(-54.23, 23.11) * mm, "construction": true});
            skLineSegment(sketch, "E127.direction2", {"start": v(-79.23, 23.11) * mm, "end": v(-79.23, 18.11) * mm, "construction": true});
            skSolve(sketch);
        }
        {
            var Q0;
            Q0 = qSketchRegion(id + "F6", true);
            extrude(context, id + "F7", {"entities" : qUnion([Q0]), "operationType" : NewBodyOperationType.REMOVE, "oppositeDirection" : true, "depth" : 25 * mm});
        }
    });
